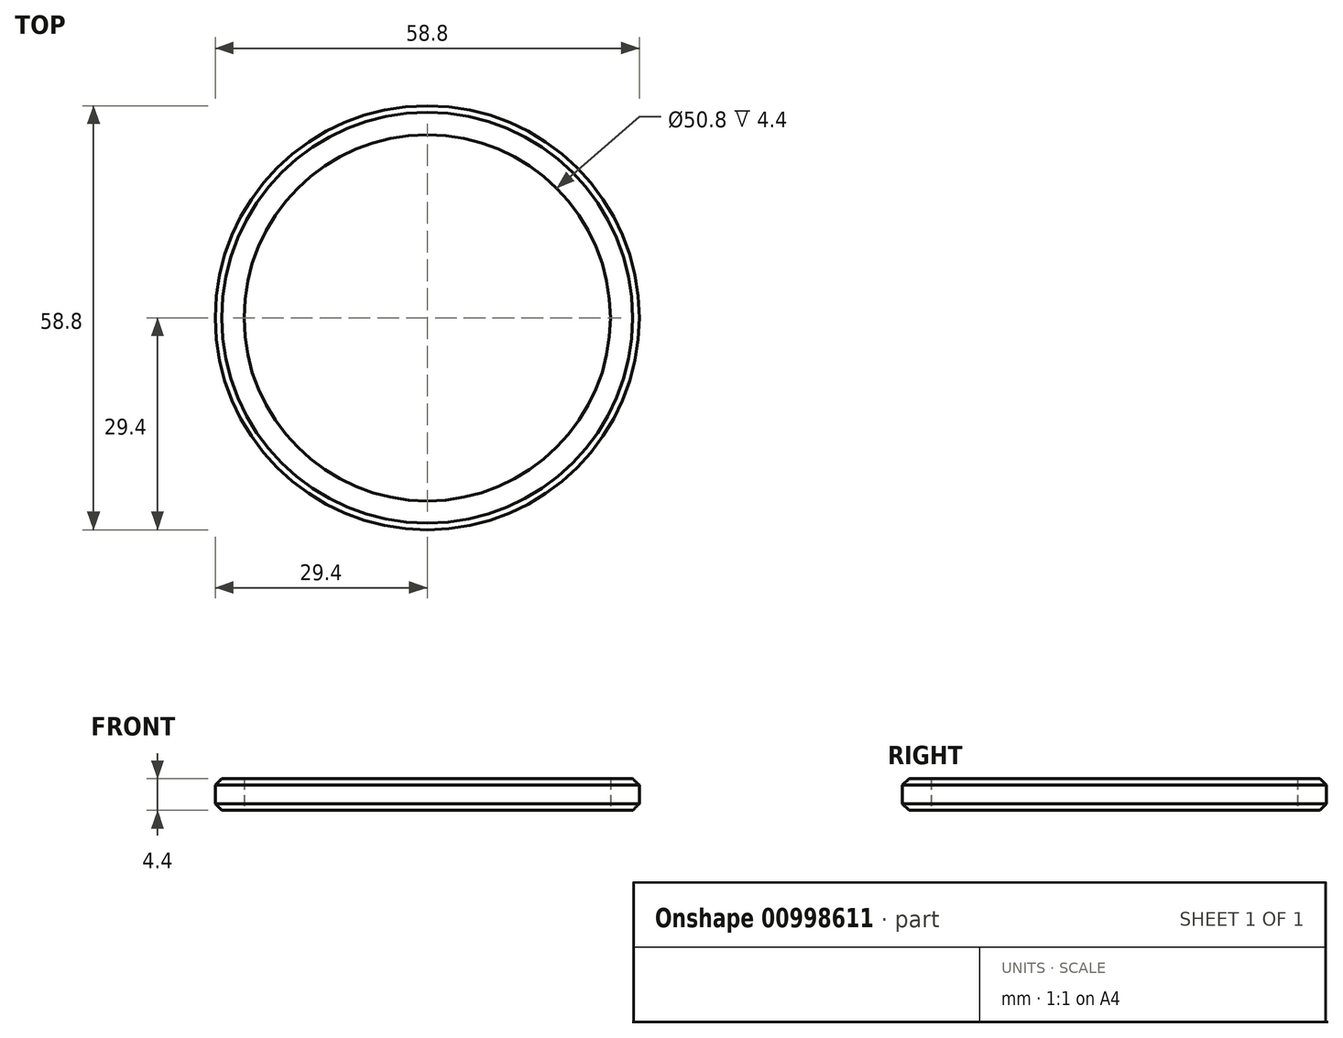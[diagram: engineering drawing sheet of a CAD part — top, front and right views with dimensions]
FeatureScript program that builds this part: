
annotation { "Feature Type Name" : "Feature", "Feature Type Description" : "" }
export const myFeature = defineFeature(function(context is Context, id is Id, definition is map)
    precondition{}
    {
        {
            var Q0;
            Q0=qCreatedBy(makeId("Top.planeOp"),FACE);
            var sketch = newSketch(context, id + "F0", { "sketchPlane" : qUnion([Q0])});
            skCircle(sketch, "E0", {"center": v(0, 0) * mm, "radius": 25.4 * mm});
            skCircle(sketch, "E1", {"center": v(0, 0) * mm, "radius": 29.4 * mm});
            skSolve(sketch);
        }
        {
            var Q0;
            Q0 = qSketchRegion(id + "F0", true);
            extrude(context, id + "F1", {"entities" : qUnion([Q0]), "depth" : 4.4 * mm, "offsetDistance" : 25 * mm});
        }
        {
            var Q0;
            Q0=makeQuery(id+"F1.opExtrude","SWEPT_FACE",FACE,{"disambiguationData":[OSD([sQuery(id+"F0.wireOp",EDGE,"E1")])]});
            chamfer(context, id + "F2", {"entities" : qUnion([Q0]), "width" : .9 * mm, "tangentPropagation" : true});
        }
    });
